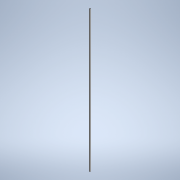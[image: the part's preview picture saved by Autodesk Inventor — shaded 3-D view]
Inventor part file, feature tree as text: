
AUTODESK INVENTOR PART (.ipt)
format: ipt  version: 2022 (Build 260153000, 153)  size: 148,992 bytes
history: native  units: mm
features: extrude x1, sketch x1
ambient origin geometry x8: Origin, YZ Plane, XZ Plane, XY Plane, X Axis, Y Axis, Z Axis, Center Point
bodies: Body1 (feature_tree)
feature tree (2):
  extrude  "Extrusion7"  Depth=5.0mm
  sketch  "Sketch4"  dims[d31=34.456mm d103=5.0mm d104=5.0mm d105=986.0mm d106=0.0mm]
